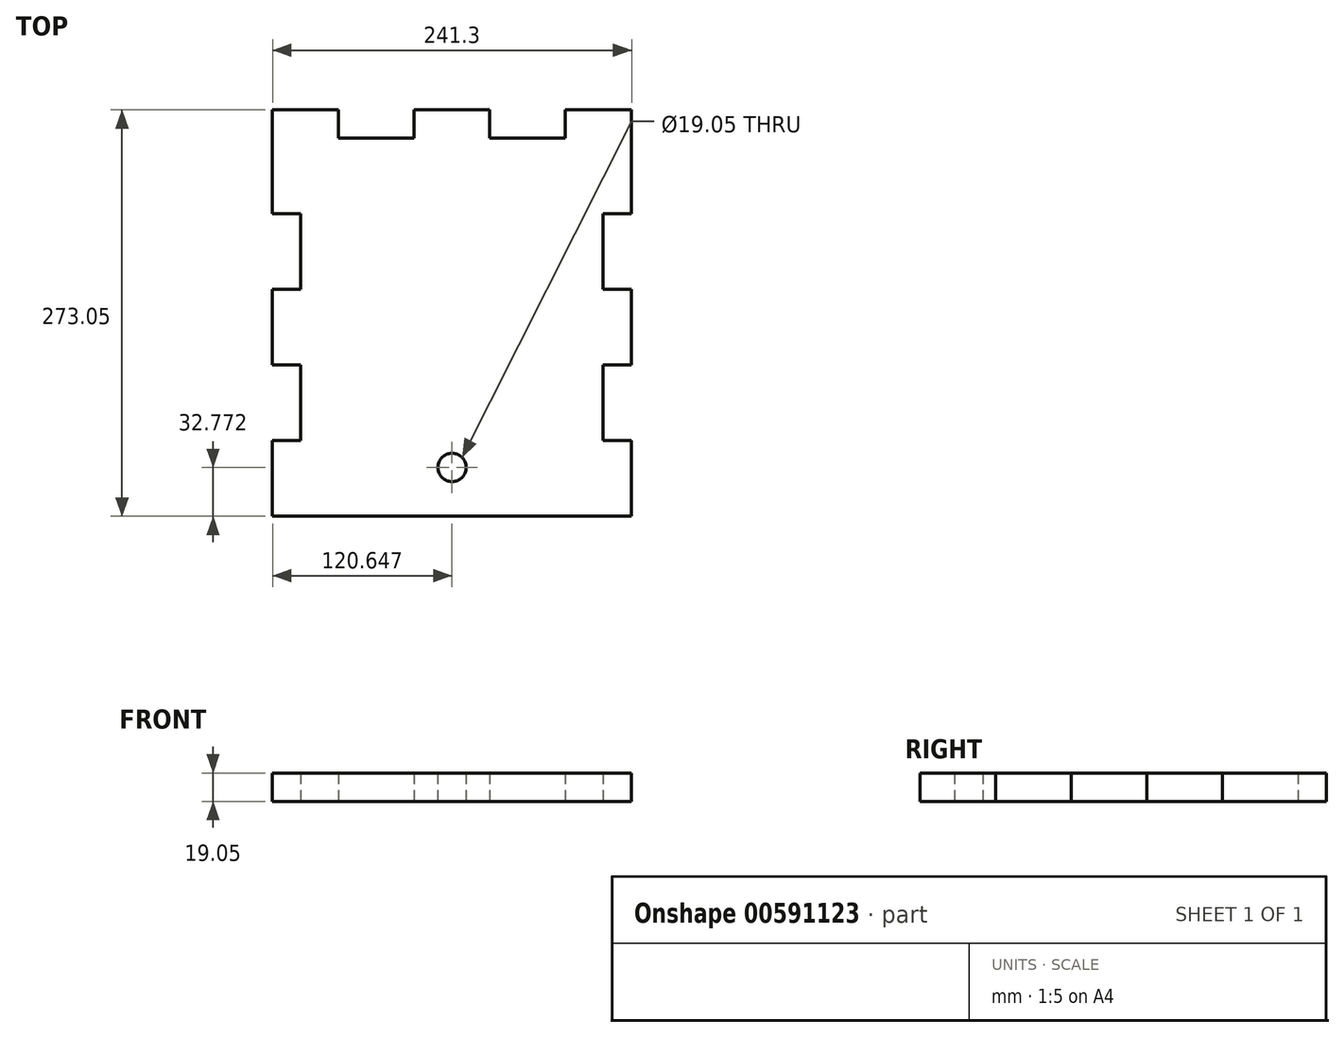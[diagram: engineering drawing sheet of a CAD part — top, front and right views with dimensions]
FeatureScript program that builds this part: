
annotation { "Feature Type Name" : "Feature", "Feature Type Description" : "" }
export const myFeature = defineFeature(function(context is Context, id is Id, definition is map)
    precondition{}
    {
        {
            var Q0;
            Q0=qCreatedBy(makeId("Top.planeOp"),FACE);
            var sketch = newSketch(context, id + "F0", { "sketchPlane" : qUnion([Q0])});
            skLineSegment(sketch, "E0.bottom", {"start": v(-98.71, 101.42) * mm, "end": v(104.49, 101.42) * mm});
            skLineSegment(sketch, "E0.top", {"start": v(-98.71, -152.58) * mm, "end": v(104.49, -152.58) * mm});
            skLineSegment(sketch, "E0.left", {"start": v(-98.71, 101.42) * mm, "end": v(-98.71, -152.58) * mm});
            skLineSegment(sketch, "E0.right", {"start": v(104.49, 101.42) * mm, "end": v(104.49, -152.58) * mm});
            skLineSegment(sketch, "E1", {"start": v(-98.71, -152.58) * mm, "end": v(-117.76, -152.58) * mm});
            skLineSegment(sketch, "E2", {"start": v(-117.76, -152.58) * mm, "end": v(-117.76, -101.78) * mm});
            skLineSegment(sketch, "E3", {"start": v(-117.76, -101.78) * mm, "end": v(-98.71, -101.78) * mm});
            skLineSegment(sketch, "E4", {"start": v(-98.71, -101.78) * mm, "end": v(-98.71, -50.98) * mm});
            skLineSegment(sketch, "E5", {"start": v(-98.71, -50.98) * mm, "end": v(-117.76, -50.98) * mm});
            skLineSegment(sketch, "E6", {"start": v(-117.76, -50.98) * mm, "end": v(-117.76, -0.18) * mm});
            skLineSegment(sketch, "E7", {"start": v(-117.76, -0.18) * mm, "end": v(-98.71, -0.18) * mm});
            skLineSegment(sketch, "E8", {"start": v(-98.71, -0.18) * mm, "end": v(-98.71, 50.62) * mm});
            skLineSegment(sketch, "E9", {"start": v(-98.71, 50.62) * mm, "end": v(-117.76, 50.62) * mm});
            skLineSegment(sketch, "E10", {"start": v(-117.76, 50.62) * mm, "end": v(-117.76, 101.42) * mm});
            skLineSegment(sketch, "E11", {"start": v(-117.76, 101.42) * mm, "end": v(-98.71, 101.42) * mm});
            skLineSegment(sketch, "E12", {"start": v(2.89, 101.42) * mm, "end": v(2.89, -152.58) * mm, "construction": true});
            skLineSegment(sketch, "E13.MirrorCS", {"start": v(123.54, 101.42) * mm, "end": v(104.49, 101.42) * mm});
            skLineSegment(sketch, "E14.MirrorCS", {"start": v(123.54, 50.62) * mm, "end": v(123.54, 101.42) * mm});
            skLineSegment(sketch, "E15.MirrorCS", {"start": v(104.49, 50.62) * mm, "end": v(123.54, 50.62) * mm});
            skLineSegment(sketch, "E16.MirrorCS", {"start": v(123.54, -0.18) * mm, "end": v(104.49, -0.18) * mm});
            skLineSegment(sketch, "E17.MirrorCS", {"start": v(123.54, -50.98) * mm, "end": v(123.54, -0.18) * mm});
            skLineSegment(sketch, "E18.MirrorCS", {"start": v(104.49, -50.98) * mm, "end": v(123.54, -50.98) * mm});
            skLineSegment(sketch, "E19.MirrorCS", {"start": v(123.54, -101.78) * mm, "end": v(104.49, -101.78) * mm});
            skLineSegment(sketch, "E20.MirrorCS", {"start": v(123.54, -152.58) * mm, "end": v(123.54, -101.78) * mm});
            skLineSegment(sketch, "E21.MirrorCS", {"start": v(104.49, -152.58) * mm, "end": v(123.54, -152.58) * mm});
            skLineSegment(sketch, "E22", {"start": v(-98.71, 101.42) * mm, "end": v(-98.71, 120.47) * mm});
            skLineSegment(sketch, "E23", {"start": v(-98.71, 120.47) * mm, "end": v(-73.31, 120.47) * mm});
            skLineSegment(sketch, "E24", {"start": v(-73.31, 120.47) * mm, "end": v(-73.31, 101.42) * mm});
            skLineSegment(sketch, "E25", {"start": v(-73.31, 101.42) * mm, "end": v(-22.51, 101.42) * mm});
            skLineSegment(sketch, "E26", {"start": v(-22.51, 101.42) * mm, "end": v(-22.51, 120.47) * mm});
            skLineSegment(sketch, "E27", {"start": v(-22.51, 120.47) * mm, "end": v(28.29, 120.47) * mm});
            skLineSegment(sketch, "E28", {"start": v(28.29, 120.47) * mm, "end": v(28.29, 101.42) * mm});
            skLineSegment(sketch, "E29", {"start": v(28.29, 101.42) * mm, "end": v(79.09, 101.42) * mm});
            skLineSegment(sketch, "E30", {"start": v(79.09, 101.42) * mm, "end": v(79.09, 120.47) * mm});
            skLineSegment(sketch, "E31", {"start": v(79.09, 120.47) * mm, "end": v(104.49, 120.47) * mm});
            skLineSegment(sketch, "E32", {"start": v(104.49, 120.47) * mm, "end": v(104.49, 101.42) * mm});
            skCircle(sketch, "E33", {"center": v(2.89, -119.8) * mm, "radius": 9.53 * mm, "construction": true});
            skCircle(sketch, "E34", {"center": v(2.89, -119.8) * mm, "radius": 9.53 * mm});
            skLineSegment(sketch, "E35", {"start": v(-98.71, 120.47) * mm, "end": v(-117.76, 120.47) * mm});
            skLineSegment(sketch, "E36", {"start": v(-117.76, 120.47) * mm, "end": v(-117.76, 101.42) * mm});
            skLineSegment(sketch, "E37", {"start": v(104.49, 120.47) * mm, "end": v(123.54, 120.47) * mm});
            skLineSegment(sketch, "E38", {"start": v(123.54, 120.47) * mm, "end": v(123.54, 101.42) * mm});
            skSolve(sketch);
        }
        {
            var Q0;
            {var subQ0=sQuery(id+"F0.wireOp",EDGE,"E1");Q0=makeQuery(id+"F0.imprint","IMPRINT",FACE,{"disambiguationData":[TD([[makeQuery(id+"F0.imprint","IMPRINT",EDGE,{"derivedFrom":subQ0}),-1.0]])]});}
            var Q1;
            {var subQ7=sQuery(id+"F0.wireOp",EDGE,"E0.top");Q1=makeQuery(id+"F0.imprint","IMPRINT",FACE,{"disambiguationData":[TD([[makeQuery(id+"F0.imprint","IMPRINT",EDGE,{"derivedFrom":subQ7}),1.0]])]});}
            var Q2;
            {var subQ0=sQuery(id+"F0.wireOp",EDGE,"E5");Q2=makeQuery(id+"F0.imprint","IMPRINT",FACE,{"disambiguationData":[TD([[makeQuery(id+"F0.imprint","IMPRINT",EDGE,{"derivedFrom":subQ0}),-1.0]])]});}
            var Q3;
            {var subQ2=sQuery(id+"F0.wireOp",EDGE,"E9");Q3=makeQuery(id+"F0.imprint","IMPRINT",FACE,{"disambiguationData":[TD([[makeQuery(id+"F0.imprint","IMPRINT",EDGE,{"derivedFrom":subQ2}),-1.0]])]});}
            var Q4;
            {var subQ0=sQuery(id+"F0.wireOp",EDGE,"E22");Q4=makeQuery(id+"F0.imprint","IMPRINT",FACE,{"disambiguationData":[TD([[makeQuery(id+"F0.imprint","IMPRINT",EDGE,{"derivedFrom":subQ0}),-1.0]])]});}
            var Q5;
            {var subQ0=sQuery(id+"F0.wireOp",EDGE,"E26");Q5=makeQuery(id+"F0.imprint","IMPRINT",FACE,{"disambiguationData":[TD([[makeQuery(id+"F0.imprint","IMPRINT",EDGE,{"derivedFrom":subQ0}),-1.0]])]});}
            var Q6;
            {var subQ2=sQuery(id+"F0.wireOp",EDGE,"E30");Q6=makeQuery(id+"F0.imprint","IMPRINT",FACE,{"disambiguationData":[TD([[makeQuery(id+"F0.imprint","IMPRINT",EDGE,{"derivedFrom":subQ2}),-1.0]])]});}
            var Q7;
            {var subQ0=sQuery(id+"F0.wireOp",EDGE,"E13.MirrorCS");Q7=makeQuery(id+"F0.imprint","IMPRINT",FACE,{"disambiguationData":[TD([[makeQuery(id+"F0.imprint","IMPRINT",EDGE,{"derivedFrom":subQ0}),1.0]])]});}
            var Q8;
            {var subQ0=sQuery(id+"F0.wireOp",EDGE,"E16.MirrorCS");Q8=makeQuery(id+"F0.imprint","IMPRINT",FACE,{"disambiguationData":[TD([[makeQuery(id+"F0.imprint","IMPRINT",EDGE,{"derivedFrom":subQ0}),1.0]])]});}
            var Q9;
            {var subQ2=sQuery(id+"F0.wireOp",EDGE,"E19.MirrorCS");Q9=makeQuery(id+"F0.imprint","IMPRINT",FACE,{"disambiguationData":[TD([[makeQuery(id+"F0.imprint","IMPRINT",EDGE,{"derivedFrom":subQ2}),1.0]])]});}
            extrude(context, id + "F1", {"entities" : qUnion([Q0, Q1, Q2, Q3, Q4, Q5, Q6, Q7, Q8, Q9]), "depth" : 19.05 * mm, "offsetDistance" : 25.4 * mm});
        }
        {
            var Q0;
            Q0 = qSketchRegion(id + "F0", true);
            extrude(context, id + "F2", {"entities" : qUnion([Q0]), "operationType" : NewBodyOperationType.ADD, "depth" : 19.05 * mm, "offsetDistance" : 25.4 * mm});
        }
    });
